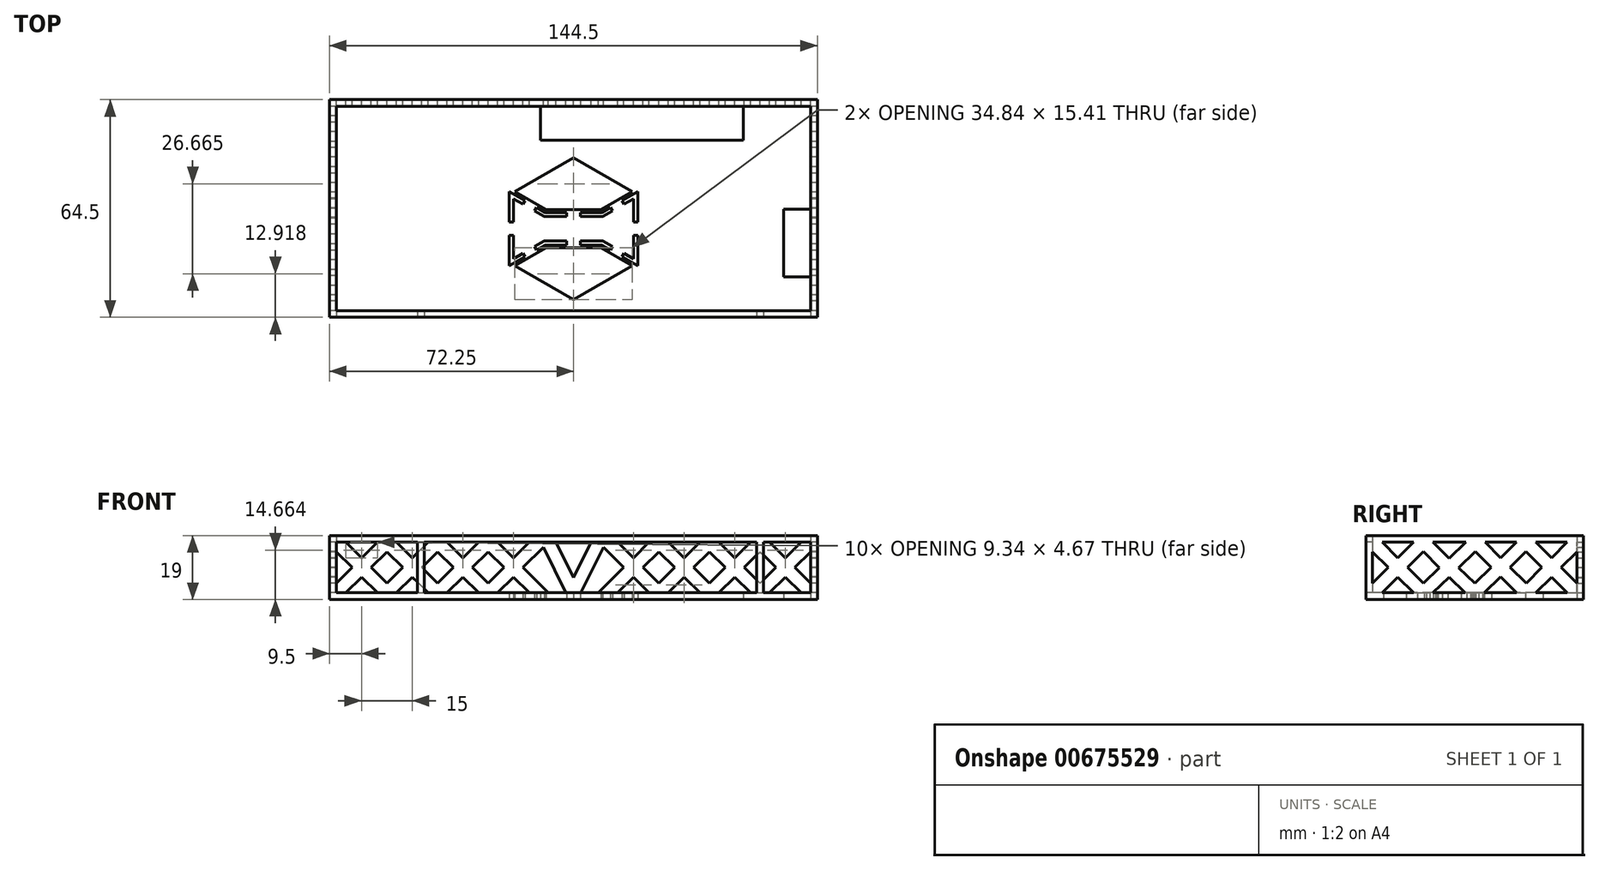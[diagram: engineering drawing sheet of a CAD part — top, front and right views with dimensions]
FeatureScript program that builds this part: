
annotation { "Feature Type Name" : "Feature", "Feature Type Description" : "" }
export const myFeature = defineFeature(function(context is Context, id is Id, definition is map)
    precondition{}
    {
        {
            var Q0;
            Q0=qCreatedBy(makeId("Top.planeOp"),FACE);
            var sketch = newSketch(context, id + "F0", { "sketchPlane" : qUnion([Q0])});
            skLineSegment(sketch, "E0.bottom", {"start": v(-72.25, 32.25) * mm, "end": v(72.25, 32.25) * mm});
            skLineSegment(sketch, "E0.top", {"start": v(-72.25, -32.25) * mm, "end": v(72.25, -32.25) * mm});
            skLineSegment(sketch, "E0.left", {"start": v(-72.25, 32.25) * mm, "end": v(-72.25, -32.25) * mm});
            skLineSegment(sketch, "E0.right", {"start": v(72.25, 32.25) * mm, "end": v(72.25, -32.25) * mm});
            skSolve(sketch);
        }
        {
            var Q0;
            Q0=qSketchRegion(id+"F0",true);
            extrude(context, id + "F1", {"entities" : qUnion([Q0]), "depth" : 2 * mm, "offsetDistance" : 25 * mm});
        }
        {
            var Q0;
            Q0=makeQuery(id+"F1.opExtrude","CAP_FACE",FACE,{"disambiguationData":[OSD([sQuery(id+"F0.wireOp",EDGE,"E0.bottom"),sQuery(id+"F0.wireOp",EDGE,"E0.top"),sQuery(id+"F0.wireOp",EDGE,"E0.left"),sQuery(id+"F0.wireOp",EDGE,"E0.right")])],"isStart":false});
            var sketch = newSketch(context, id + "F2", { "sketchPlane" : qUnion([Q0])});
            skLineSegment(sketch, "E1.0", {"start": v(-72.25, 32.25) * mm, "end": v(-72.25, -32.25) * mm});
            skLineSegment(sketch, "E1.1", {"start": v(72.25, 32.25) * mm, "end": v(-72.25, 32.25) * mm});
            skLineSegment(sketch, "E1.2", {"start": v(72.25, -32.25) * mm, "end": v(72.25, 32.25) * mm});
            skLineSegment(sketch, "E1.3", {"start": v(-72.25, -32.25) * mm, "end": v(72.25, -32.25) * mm});
            skLineSegment(sketch, "E2.0", {"start": v(-70.25, 30.25) * mm, "end": v(-70.25, -30.25) * mm});
            skLineSegment(sketch, "E2.1", {"start": v(70.25, 30.25) * mm, "end": v(-70.25, 30.25) * mm});
            skLineSegment(sketch, "E2.2", {"start": v(70.25, -30.25) * mm, "end": v(70.25, 30.25) * mm});
            skLineSegment(sketch, "E2.3", {"start": v(-70.25, -30.25) * mm, "end": v(70.25, -30.25) * mm});
            skSolve(sketch);
        }
        {
            var Q0;
            Q0=qSketchRegion(id+"F2",true);
            extrude(context, id + "F3", {"entities" : qUnion([Q0]), "operationType" : NewBodyOperationType.ADD, "depth" : 17 * mm, "offsetDistance" : 25 * mm});
        }
        {
            var Q0;
            Q0=makeQuery(id+"F3.boolean.opBoolean","MERGE",FACE,{"derivedFrom":[makeQuery(id+"F1.opExtrude","SWEPT_FACE",FACE,{"disambiguationData":[OSD([sQuery(id+"F0.wireOp",EDGE,"E0.top")])]}),makeQuery(id+"F3.opExtrude","SWEPT_FACE",FACE,{"disambiguationData":[OSD([sQuery(id+"F2.wireOp",EDGE,"E1.3")])]})]});
            var sketch = newSketch(context, id + "F4", { "sketchPlane" : qUnion([Q0])});
            skLineSegment(sketch, "E3.0", {"start": v(-70.25, 2) * mm, "end": v(-46.25, 2) * mm});
            skLineSegment(sketch, "E3.1", {"start": v(-70.25, 17) * mm, "end": v(-70.25, 2) * mm});
            skLineSegment(sketch, "E3.2", {"start": v(70.25, 17) * mm, "end": v(56.25, 17) * mm});
            skLineSegment(sketch, "E3.3", {"start": v(70.25, 2) * mm, "end": v(70.25, 17) * mm});
            skLineSegment(sketch, "E4", {"start": v(-46.25, 2) * mm, "end": v(-46.25, 17) * mm});
            skLineSegment(sketch, "E5", {"start": v(-44.25, 2) * mm, "end": v(-44.25, 17) * mm});
            skLineSegment(sketch, "E6", {"start": v(56.25, 2) * mm, "end": v(56.25, 17) * mm});
            skLineSegment(sketch, "E7", {"start": v(54.25, 2) * mm, "end": v(54.25, 17) * mm});
            skLineSegment(sketch, "E8.trimOffspring", {"start": v(54.25, 17) * mm, "end": v(-44.25, 17) * mm});
            skLineSegment(sketch, "E9.trimOffspring", {"start": v(56.25, 2) * mm, "end": v(70.25, 2) * mm});
            skLineSegment(sketch, "E10.trimOffspring", {"start": v(-46.25, 17) * mm, "end": v(-70.25, 17) * mm});
            skLineSegment(sketch, "E11.trimOffspring", {"start": v(-44.25, 2) * mm, "end": v(54.25, 2) * mm});
            skSolve(sketch);
        }
        {
            var Q0;
            Q0=qSketchRegion(id+"F4",true);
            extrude(context, id + "F5", {"entities" : qUnion([Q0]), "operationType" : NewBodyOperationType.REMOVE, "oppositeDirection" : true, "depth" : 25 * mm, "offsetDistance" : 25 * mm});
        }
        {
            var Q0;
            Q0=makeQuery(id+"F1.opExtrude","CAP_FACE",FACE,{"disambiguationData":[OSD([sQuery(id+"F0.wireOp",EDGE,"E0.bottom"),sQuery(id+"F0.wireOp",EDGE,"E0.top"),sQuery(id+"F0.wireOp",EDGE,"E0.left"),sQuery(id+"F0.wireOp",EDGE,"E0.right")])],"isStart":true});
            var sketch = newSketch(context, id + "F6", { "sketchPlane" : qUnion([Q0])});
            skLineSegment(sketch, "E12.0", {"start": v(-70.25, 30.25) * mm, "end": v(-70.25, -30.25) * mm, "construction": true});
            skLineSegment(sketch, "E12.1", {"start": v(70.25, 30.25) * mm, "end": v(-70.25, 30.25) * mm, "construction": true});
            skLineSegment(sketch, "E12.3", {"start": v(-9.75, -30.25) * mm, "end": v(50.25, -30.25) * mm});
            skLineSegment(sketch, "E13", {"start": v(50.25, -30.25) * mm, "end": v(50.25, -20.25) * mm});
            skLineSegment(sketch, "E14", {"start": v(-9.75, -30.25) * mm, "end": v(-9.75, -20.25) * mm});
            skLineSegment(sketch, "E15", {"start": v(-9.75, -20.25) * mm, "end": v(50.25, -20.25) * mm});
            skLineSegment(sketch, "E16", {"start": v(50.25, -30.25) * mm, "end": v(70.25, -30.25) * mm, "construction": true});
            skLineSegment(sketch, "E17", {"start": v(-9.75, -30.25) * mm, "end": v(-70.25, -30.25) * mm, "construction": true});
            skLineSegment(sketch, "E18", {"start": v(70.25, 20.25) * mm, "end": v(62.25, 20.25) * mm});
            skLineSegment(sketch, "E19", {"start": v(70.25, 0.25) * mm, "end": v(62.25, 0.25) * mm});
            skLineSegment(sketch, "E20", {"start": v(70.25, -30.25) * mm, "end": v(70.25, 0.25) * mm, "construction": true});
            skLineSegment(sketch, "E21", {"start": v(70.25, 20.25) * mm, "end": v(70.25, 30.25) * mm, "construction": true});
            skLineSegment(sketch, "E22", {"start": v(70.25, 20.25) * mm, "end": v(70.25, 0.25) * mm});
            skLineSegment(sketch, "E23", {"start": v(62.25, 0.25) * mm, "end": v(62.25, 20.25) * mm});
            skSolve(sketch);
        }
        {
            var Q0;
            Q0=qSketchRegion(id+"F6",true);
            extrude(context, id + "F7", {"entities" : qUnion([Q0]), "operationType" : NewBodyOperationType.REMOVE, "oppositeDirection" : true, "depth" : 25 * mm, "offsetDistance" : 25 * mm});
        }
        {
            var Q0;
            Q0=makeQuery(id+"F3.boolean.opBoolean","MERGE",FACE,{"derivedFrom":[makeQuery(id+"F1.opExtrude","SWEPT_FACE",FACE,{"disambiguationData":[OSD([sQuery(id+"F0.wireOp",EDGE,"E0.left")])]}),makeQuery(id+"F3.opExtrude","SWEPT_FACE",FACE,{"disambiguationData":[OSD([sQuery(id+"F2.wireOp",EDGE,"E1.0")])]})]});
            var sketch = newSketch(context, id + "F8", { "sketchPlane" : qUnion([Q0])});
            skLineSegment(sketch, "E24.0", {"start": v(-27.42, 2) * mm, "end": v(-18.08, 2) * mm});
            skLineSegment(sketch, "E24.1", {"start": v(-30.25, 14.17) * mm, "end": v(-30.25, 4.83) * mm});
            skLineSegment(sketch, "E24.3", {"start": v(30.25, 4.83) * mm, "end": v(30.25, 14.17) * mm});
            skLineSegment(sketch, "E25", {"start": v(-27.42, 17) * mm, "end": v(-18.08, 17) * mm});
            skLineSegment(sketch, "E26", {"start": v(-12.4, 17) * mm, "end": v(-3.08, 17) * mm});
            skLineSegment(sketch, "E27", {"start": v(2.63, 17) * mm, "end": v(12.4, 17) * mm});
            skLineSegment(sketch, "E28", {"start": v(18.08, 17) * mm, "end": v(27.42, 17) * mm});
            skLineSegment(sketch, "E29", {"start": v(-30.25, 2) * mm, "end": v(-15.25, 17) * mm, "construction": true});
            skLineSegment(sketch, "E30", {"start": v(-15.25, 17) * mm, "end": v(0, 2) * mm, "construction": true});
            skLineSegment(sketch, "E31", {"start": v(0, 2) * mm, "end": v(15.25, 17) * mm, "construction": true});
            skLineSegment(sketch, "E32", {"start": v(15.25, 17) * mm, "end": v(30.25, 2) * mm, "construction": true});
            skLineSegment(sketch, "E33", {"start": v(15.25, 17) * mm, "end": v(15.25, 2) * mm, "construction": true});
            skLineSegment(sketch, "E34", {"start": v(-0.25, 17) * mm, "end": v(0, 2) * mm, "construction": true});
            skLineSegment(sketch, "E35", {"start": v(-15.25, 17) * mm, "end": v(-15.25, 2) * mm, "construction": true});
            skLineSegment(sketch, "E36", {"start": v(-30.25, 17) * mm, "end": v(-15.25, 2) * mm, "construction": true});
            skLineSegment(sketch, "E37", {"start": v(-0.25, 17) * mm, "end": v(-15.25, 2) * mm, "construction": true});
            skLineSegment(sketch, "E38", {"start": v(30.25, 17) * mm, "end": v(15.25, 2) * mm, "construction": true});
            skLineSegment(sketch, "E39", {"start": v(-0.25, 17) * mm, "end": v(15.25, 2) * mm, "construction": true});
            skLineSegment(sketch, "E40.0", {"start": v(-27.42, 17) * mm, "end": v(-22.75, 12.33) * mm});
            skLineSegment(sketch, "E40.1", {"start": v(-3.08, 17) * mm, "end": v(-7.7, 12.38) * mm});
            skLineSegment(sketch, "E40.2", {"start": v(2.63, 17) * mm, "end": v(7.55, 12.23) * mm});
            skLineSegment(sketch, "E40.3", {"start": v(27.42, 17) * mm, "end": v(22.75, 12.33) * mm});
            skLineSegment(sketch, "E41.0", {"start": v(-30.25, 14.17) * mm, "end": v(-25.58, 9.5) * mm});
            skLineSegment(sketch, "E41.1", {"start": v(-0.23, 14.2) * mm, "end": v(-4.85, 9.57) * mm});
            skLineSegment(sketch, "E41.2", {"start": v(-0.23, 14.2) * mm, "end": v(4.7, 9.43) * mm});
            skLineSegment(sketch, "E41.3", {"start": v(30.25, 14.17) * mm, "end": v(18.08, 2) * mm});
            skLineSegment(sketch, "E42.0", {"start": v(15.24, 14.18) * mm, "end": v(19.92, 9.5) * mm});
            skLineSegment(sketch, "E42.1", {"start": v(2.85, 2) * mm, "end": v(7.57, 6.64) * mm});
            skLineSegment(sketch, "E42.2", {"start": v(-15.24, 14.18) * mm, "end": v(-10.53, 9.55) * mm});
            skLineSegment(sketch, "E42.3", {"start": v(-27.42, 2) * mm, "end": v(-22.75, 6.67) * mm});
            skLineSegment(sketch, "E43.0", {"start": v(18.08, 17) * mm, "end": v(22.75, 12.33) * mm});
            skLineSegment(sketch, "E43.1", {"start": v(0, 4.8) * mm, "end": v(4.7, 9.43) * mm});
            skLineSegment(sketch, "E43.2", {"start": v(-12.4, 17) * mm, "end": v(-7.7, 12.38) * mm});
            skLineSegment(sketch, "E43.3", {"start": v(-30.25, 4.83) * mm, "end": v(-25.58, 9.5) * mm});
            skLineSegment(sketch, "E44.trimOffspring", {"start": v(7.55, 12.23) * mm, "end": v(12.4, 17) * mm});
            skLineSegment(sketch, "E45.trimOffspring", {"start": v(7.57, 6.64) * mm, "end": v(12.37, 2) * mm});
            skLineSegment(sketch, "E46.trimOffspring", {"start": v(10.43, 9.45) * mm, "end": v(15.23, 4.8) * mm});
            skLineSegment(sketch, "E47.trimOffspring", {"start": v(22.75, 6.67) * mm, "end": v(27.42, 2) * mm});
            skLineSegment(sketch, "E48.trimOffspring", {"start": v(19.92, 9.5) * mm, "end": v(15.23, 4.8) * mm});
            skLineSegment(sketch, "E49.trimOffspring", {"start": v(25.58, 9.5) * mm, "end": v(30.25, 4.83) * mm});
            skLineSegment(sketch, "E50.trimOffspring", {"start": v(10.43, 9.45) * mm, "end": v(15.24, 14.18) * mm});
            skLineSegment(sketch, "E51.trimOffspring", {"start": v(-7.68, 6.75) * mm, "end": v(-2.85, 2) * mm});
            skLineSegment(sketch, "E52.trimOffspring", {"start": v(-7.68, 6.75) * mm, "end": v(-12.42, 2) * mm});
            skLineSegment(sketch, "E53.trimOffspring", {"start": v(-4.85, 9.57) * mm, "end": v(0, 4.8) * mm});
            skLineSegment(sketch, "E54.trimOffspring", {"start": v(-10.53, 9.55) * mm, "end": v(-15.25, 4.83) * mm});
            skLineSegment(sketch, "E55.trimOffspring", {"start": v(-19.92, 9.5) * mm, "end": v(-15.25, 4.83) * mm});
            skLineSegment(sketch, "E56.trimOffspring", {"start": v(-22.75, 12.33) * mm, "end": v(-18.08, 17) * mm});
            skLineSegment(sketch, "E57.trimOffspring", {"start": v(-22.75, 6.67) * mm, "end": v(-18.08, 2) * mm});
            skLineSegment(sketch, "E58.trimOffspring", {"start": v(-19.92, 9.5) * mm, "end": v(-15.24, 14.18) * mm});
            skLineSegment(sketch, "E59.trimOffspring", {"start": v(-12.42, 2) * mm, "end": v(-2.85, 2) * mm});
            skLineSegment(sketch, "E60.trimOffspring", {"start": v(2.85, 2) * mm, "end": v(12.37, 2) * mm});
            skLineSegment(sketch, "E61.trimOffspring", {"start": v(18.08, 2) * mm, "end": v(27.42, 2) * mm});
            skSolve(sketch);
        }
        {
            var Q0;
            Q0=qSketchRegion(id+"F8",true);
            extrude(context, id + "F9", {"entities" : qUnion([Q0]), "operationType" : NewBodyOperationType.REMOVE, "endBound" : BoundingType.THROUGH_ALL, "oppositeDirection" : true, "depth" : 25 * mm, "offsetDistance" : 25 * mm});
        }
        {
            var Q0;
            Q0=makeQuery(id+"F3.boolean.opBoolean","MERGE",FACE,{"derivedFrom":[makeQuery(id+"F1.opExtrude","SWEPT_FACE",FACE,{"disambiguationData":[OSD([sQuery(id+"F0.wireOp",EDGE,"E0.bottom")])]}),makeQuery(id+"F3.opExtrude","SWEPT_FACE",FACE,{"disambiguationData":[OSD([sQuery(id+"F2.wireOp",EDGE,"E1.1")])]})]});
            var sketch = newSketch(context, id + "F10", { "sketchPlane" : qUnion([Q0])});
            skLineSegment(sketch, "E62.0", {"start": v(-67.42, 2) * mm, "end": v(-58.08, 2) * mm});
            skLineSegment(sketch, "E62.1", {"start": v(-70.25, 14.17) * mm, "end": v(-70.25, 4.83) * mm});
            skLineSegment(sketch, "E62.2", {"start": v(67.42, 17) * mm, "end": v(58.08, 17) * mm});
            skLineSegment(sketch, "E62.3", {"start": v(70.25, 4.83) * mm, "end": v(70.25, 14.17) * mm});
            skLineSegment(sketch, "E63", {"start": v(0, 17) * mm, "end": v(0, 2) * mm, "construction": true});
            skLineSegment(sketch, "E64", {"start": v(-70.25, 17) * mm, "end": v(-55.25, 2) * mm, "construction": true});
            skLineSegment(sketch, "E65", {"start": v(-55.25, 2) * mm, "end": v(-40.25, 17) * mm, "construction": true});
            skLineSegment(sketch, "E66", {"start": v(-40.25, 17) * mm, "end": v(-25.25, 2) * mm, "construction": true});
            skLineSegment(sketch, "E67", {"start": v(-25.25, 2) * mm, "end": v(-10.25, 17) * mm, "construction": true});
            skLineSegment(sketch, "E68", {"start": v(70.25, 17) * mm, "end": v(55.25, 2) * mm, "construction": true});
            skLineSegment(sketch, "E69", {"start": v(55.25, 2) * mm, "end": v(40.25, 17) * mm, "construction": true});
            skLineSegment(sketch, "E70", {"start": v(40.25, 17) * mm, "end": v(25.25, 2) * mm, "construction": true});
            skLineSegment(sketch, "E71", {"start": v(25.25, 2) * mm, "end": v(10.25, 17) * mm, "construction": true});
            skLineSegment(sketch, "E72", {"start": v(-70.25, 2) * mm, "end": v(-55.25, 17) * mm, "construction": true});
            skLineSegment(sketch, "E73", {"start": v(-55.25, 17) * mm, "end": v(-40.25, 2) * mm, "construction": true});
            skLineSegment(sketch, "E74", {"start": v(-40.25, 2) * mm, "end": v(-25.25, 17) * mm, "construction": true});
            skLineSegment(sketch, "E75", {"start": v(-25.25, 17) * mm, "end": v(-10.25, 2) * mm, "construction": true});
            skLineSegment(sketch, "E76", {"start": v(70.25, 2) * mm, "end": v(55.25, 17) * mm, "construction": true});
            skLineSegment(sketch, "E77", {"start": v(55.25, 17) * mm, "end": v(40.25, 2) * mm, "construction": true});
            skLineSegment(sketch, "E78", {"start": v(40.25, 2) * mm, "end": v(25.25, 17) * mm, "construction": true});
            skLineSegment(sketch, "E79", {"start": v(25.25, 17) * mm, "end": v(10.25, 2) * mm, "construction": true});
            skLineSegment(sketch, "E80.0", {"start": v(-22.42, 2) * mm, "end": v(-17.75, 6.67) * mm});
            skLineSegment(sketch, "E80.1", {"start": v(-40.25, 14.17) * mm, "end": v(-35.58, 9.5) * mm});
            skLineSegment(sketch, "E80.2", {"start": v(-52.42, 2) * mm, "end": v(-47.75, 6.67) * mm});
            skLineSegment(sketch, "E80.3", {"start": v(-70.25, 14.17) * mm, "end": v(-65.58, 9.5) * mm});
            skLineSegment(sketch, "E81.0", {"start": v(-25.25, 4.83) * mm, "end": v(-20.58, 9.5) * mm});
            skLineSegment(sketch, "E81.1", {"start": v(-37.42, 17) * mm, "end": v(-32.75, 12.33) * mm});
            skLineSegment(sketch, "E81.2", {"start": v(-55.25, 4.83) * mm, "end": v(-50.58, 9.5) * mm});
            skLineSegment(sketch, "E81.3", {"start": v(-67.42, 17) * mm, "end": v(-62.75, 12.33) * mm});
            skLineSegment(sketch, "E82.0", {"start": v(-25.25, 14.17) * mm, "end": v(-20.58, 9.5) * mm});
            skLineSegment(sketch, "E82.1", {"start": v(-37.42, 2) * mm, "end": v(-25.25, 14.17) * mm});
            skLineSegment(sketch, "E82.2", {"start": v(-55.25, 14.17) * mm, "end": v(-50.58, 9.5) * mm});
            skLineSegment(sketch, "E82.3", {"start": v(-67.42, 2) * mm, "end": v(-62.75, 6.67) * mm});
            skLineSegment(sketch, "E83.0", {"start": v(-22.42, 17) * mm, "end": v(-17.75, 12.33) * mm});
            skLineSegment(sketch, "E83.1", {"start": v(-40.25, 4.83) * mm, "end": v(-35.58, 9.5) * mm});
            skLineSegment(sketch, "E83.2", {"start": v(-52.42, 17) * mm, "end": v(-47.75, 12.33) * mm});
            skLineSegment(sketch, "E83.3", {"start": v(-70.25, 4.83) * mm, "end": v(-65.58, 9.5) * mm});
            skLineSegment(sketch, "E84.0", {"start": v(25.25, 4.83) * mm, "end": v(20.58, 9.5) * mm});
            skLineSegment(sketch, "E84.1", {"start": v(37.42, 17) * mm, "end": v(32.75, 12.33) * mm});
            skLineSegment(sketch, "E84.2", {"start": v(55.25, 4.83) * mm, "end": v(50.58, 9.5) * mm});
            skLineSegment(sketch, "E84.3", {"start": v(67.42, 17) * mm, "end": v(62.75, 12.33) * mm});
            skLineSegment(sketch, "E85.0", {"start": v(22.42, 2) * mm, "end": v(17.75, 6.67) * mm});
            skLineSegment(sketch, "E85.1", {"start": v(40.25, 14.17) * mm, "end": v(35.58, 9.5) * mm});
            skLineSegment(sketch, "E85.2", {"start": v(52.42, 2) * mm, "end": v(47.75, 6.67) * mm});
            skLineSegment(sketch, "E85.3", {"start": v(70.25, 14.17) * mm, "end": v(65.58, 9.5) * mm});
            skLineSegment(sketch, "E86.0", {"start": v(22.42, 17) * mm, "end": v(17.75, 12.33) * mm});
            skLineSegment(sketch, "E86.1", {"start": v(40.25, 4.83) * mm, "end": v(35.58, 9.5) * mm});
            skLineSegment(sketch, "E86.2", {"start": v(52.42, 17) * mm, "end": v(47.75, 12.33) * mm});
            skLineSegment(sketch, "E86.3", {"start": v(70.25, 4.83) * mm, "end": v(65.58, 9.5) * mm});
            skLineSegment(sketch, "E87.0", {"start": v(25.25, 14.17) * mm, "end": v(20.58, 9.5) * mm});
            skLineSegment(sketch, "E87.1", {"start": v(37.42, 2) * mm, "end": v(32.75, 6.67) * mm});
            skLineSegment(sketch, "E87.2", {"start": v(55.25, 14.17) * mm, "end": v(50.58, 9.5) * mm});
            skLineSegment(sketch, "E87.3", {"start": v(67.42, 2) * mm, "end": v(62.75, 6.67) * mm});
            skLineSegment(sketch, "E88.trimOffspring", {"start": v(-19.16, 8.09) * mm, "end": v(-13.08, 2) * mm});
            skLineSegment(sketch, "E89.trimOffspring", {"start": v(-17.75, 12.33) * mm, "end": v(-13.08, 17) * mm});
            skLineSegment(sketch, "E90.trimOffspring", {"start": v(-14.92, 9.5) * mm, "end": v(-7.42, 2) * mm});
            skLineSegment(sketch, "E91.trimOffspring", {"start": v(-14.92, 9.5) * mm, "end": v(-8.91, 15.5) * mm});
            skLineSegment(sketch, "E92.trimOffspring", {"start": v(-32.75, 6.67) * mm, "end": v(-28.08, 2) * mm});
            skLineSegment(sketch, "E93.trimOffspring", {"start": v(-32.75, 12.33) * mm, "end": v(-28.08, 17) * mm});
            skLineSegment(sketch, "E94.trimOffspring", {"start": v(-29.92, 9.5) * mm, "end": v(-25.25, 4.83) * mm});
            skLineSegment(sketch, "E95.trimOffspring", {"start": v(-47.75, 6.67) * mm, "end": v(-43.08, 2) * mm});
            skLineSegment(sketch, "E96.trimOffspring", {"start": v(-47.75, 12.33) * mm, "end": v(-43.08, 17) * mm});
            skLineSegment(sketch, "E97.trimOffspring", {"start": v(-44.92, 9.5) * mm, "end": v(-40.25, 4.83) * mm});
            skLineSegment(sketch, "E98.trimOffspring", {"start": v(-44.92, 9.5) * mm, "end": v(-40.25, 14.17) * mm});
            skLineSegment(sketch, "E99.trimOffspring", {"start": v(-59.92, 9.5) * mm, "end": v(-55.25, 4.83) * mm});
            skLineSegment(sketch, "E100.trimOffspring", {"start": v(-59.92, 9.5) * mm, "end": v(-55.25, 14.17) * mm});
            skLineSegment(sketch, "E101.trimOffspring", {"start": v(-62.75, 6.67) * mm, "end": v(-58.08, 2) * mm});
            skLineSegment(sketch, "E102.trimOffspring", {"start": v(-62.75, 12.33) * mm, "end": v(-58.08, 17) * mm});
            skLineSegment(sketch, "E103.trimOffspring", {"start": v(14.92, 9.5) * mm, "end": v(8.91, 15.5) * mm});
            skLineSegment(sketch, "E104.trimOffspring", {"start": v(17.75, 6.67) * mm, "end": v(13.08, 2) * mm});
            skLineSegment(sketch, "E105.trimOffspring", {"start": v(17.75, 12.33) * mm, "end": v(13.08, 17) * mm});
            skLineSegment(sketch, "E106.trimOffspring", {"start": v(14.92, 9.5) * mm, "end": v(7.42, 2) * mm});
            skLineSegment(sketch, "E107.trimOffspring", {"start": v(29.92, 9.5) * mm, "end": v(25.25, 14.17) * mm});
            skLineSegment(sketch, "E108.trimOffspring", {"start": v(32.75, 6.67) * mm, "end": v(28.08, 2) * mm});
            skLineSegment(sketch, "E109.trimOffspring", {"start": v(32.75, 12.33) * mm, "end": v(28.08, 17) * mm});
            skLineSegment(sketch, "E110.trimOffspring", {"start": v(29.92, 9.5) * mm, "end": v(25.25, 4.83) * mm});
            skLineSegment(sketch, "E111.trimOffspring", {"start": v(44.92, 9.5) * mm, "end": v(40.25, 14.17) * mm});
            skLineSegment(sketch, "E112.trimOffspring", {"start": v(47.75, 6.67) * mm, "end": v(43.08, 2) * mm});
            skLineSegment(sketch, "E113.trimOffspring", {"start": v(47.75, 12.33) * mm, "end": v(43.08, 17) * mm});
            skLineSegment(sketch, "E114.trimOffspring", {"start": v(44.92, 9.5) * mm, "end": v(40.25, 4.83) * mm});
            skLineSegment(sketch, "E115.trimOffspring", {"start": v(59.92, 9.5) * mm, "end": v(55.25, 4.83) * mm});
            skLineSegment(sketch, "E116.trimOffspring", {"start": v(62.75, 12.33) * mm, "end": v(58.08, 17) * mm});
            skLineSegment(sketch, "E117.trimOffspring", {"start": v(62.75, 6.67) * mm, "end": v(58.08, 2) * mm});
            skLineSegment(sketch, "E118.trimOffspring", {"start": v(59.92, 9.5) * mm, "end": v(55.25, 14.17) * mm});
            skLineSegment(sketch, "E119.trimOffspring", {"start": v(28.08, 2) * mm, "end": v(37.42, 2) * mm});
            skLineSegment(sketch, "E120.trimOffspring", {"start": v(13.08, 2) * mm, "end": v(22.42, 2) * mm});
            skLineSegment(sketch, "E121.trimOffspring", {"start": v(5.2, 17) * mm, "end": v(-5.2, 17) * mm});
            skLineSegment(sketch, "E122.trimOffspring", {"start": v(22.42, 17) * mm, "end": v(13.08, 17) * mm});
            skLineSegment(sketch, "E123.trimOffspring", {"start": v(37.42, 17) * mm, "end": v(28.08, 17) * mm});
            skLineSegment(sketch, "E124.trimOffspring", {"start": v(43.08, 2) * mm, "end": v(52.42, 2) * mm});
            skLineSegment(sketch, "E125.trimOffspring", {"start": v(58.08, 2) * mm, "end": v(67.42, 2) * mm});
            skLineSegment(sketch, "E126.trimOffspring", {"start": v(52.42, 17) * mm, "end": v(43.08, 17) * mm});
            skLineSegment(sketch, "E127.trimOffspring", {"start": v(-7.42, 2) * mm, "end": v(-2.23, 2) * mm});
            skLineSegment(sketch, "E128.trimOffspring", {"start": v(-22.42, 2) * mm, "end": v(-13.08, 2) * mm});
            skLineSegment(sketch, "E129.trimOffspring", {"start": v(-37.42, 2) * mm, "end": v(-28.08, 2) * mm});
            skLineSegment(sketch, "E130.trimOffspring", {"start": v(-52.42, 2) * mm, "end": v(-43.08, 2) * mm});
            skLineSegment(sketch, "E131.trimOffspring", {"start": v(-58.08, 17) * mm, "end": v(-67.42, 17) * mm});
            skLineSegment(sketch, "E132.trimOffspring", {"start": v(-43.08, 17) * mm, "end": v(-52.42, 17) * mm});
            skLineSegment(sketch, "E133.trimOffspring", {"start": v(-28.08, 17) * mm, "end": v(-37.42, 17) * mm});
            skLineSegment(sketch, "E134.trimOffspring", {"start": v(-13.08, 17) * mm, "end": v(-22.42, 17) * mm});
            skLineSegment(sketch, "E135", {"start": v(-7.42, 17) * mm, "end": v(0, 2) * mm, "construction": true});
            skLineSegment(sketch, "E136", {"start": v(7.42, 17) * mm, "end": v(0, 2) * mm, "construction": true});
            skLineSegment(sketch, "E137.0", {"start": v(5.2, 17) * mm, "end": v(0, 6.5) * mm});
            skLineSegment(sketch, "E137.1", {"start": v(-5.2, 17) * mm, "end": v(0, 6.5) * mm});
            skLineSegment(sketch, "E138.0", {"start": v(8.91, 15.5) * mm, "end": v(2.23, 2) * mm});
            skLineSegment(sketch, "E138.1", {"start": v(-8.91, 15.5) * mm, "end": v(-2.23, 2) * mm});
            skLineSegment(sketch, "E139.trimOffspring", {"start": v(2.23, 2) * mm, "end": v(7.42, 2) * mm});
            skSolve(sketch);
        }
        {
            var Q0;
            Q0=qSketchRegion(id+"F10",true);
            extrude(context, id + "F11", {"entities" : qUnion([Q0]), "operationType" : NewBodyOperationType.REMOVE, "oppositeDirection" : true, "depth" : 25 * mm, "offsetDistance" : 25 * mm});
        }
        {
            var Q0;
            {var subQ0=sQuery(id+"F0.wireOp",EDGE,"E0.top");var subQ1=sQuery(id+"F0.wireOp",EDGE,"E0.right");var subQ2=sQuery(id+"F0.wireOp",EDGE,"E0.bottom");var subQ3=sQuery(id+"F0.wireOp",EDGE,"E0.left");Q0=makeQuery(id+"FJUS3B1TuTwB0FU_1.boolean.opBoolean","SPLIT",FACE,{"disambiguationData":[TD([makeQuery(id+"F1.opExtrude","SWEPT_FACE",FACE,{"disambiguationData":[OSD([subQ2])]})])],"derivedFrom":makeQuery(id+"F1.opExtrude","CAP_FACE",FACE,{"disambiguationData":[OSD([subQ2,subQ0,subQ3,subQ1])],"isStart":true})});}
            var sketch = newSketch(context, id + "F12", { "sketchPlane" : qUnion([Q0])});
            skLineSegment(sketch, "E140.1", {"start": v(9.5, 11.5) * mm, "end": v(9.5, 0.5) * mm});
            skLineSegment(sketch, "E140.4", {"start": v(-9.5, 0.5) * mm, "end": v(-9.5, 11.5) * mm});
            skLineSegment(sketch, "E141", {"start": v(-9.5, 11.5) * mm, "end": v(-4.18, 8.41) * mm});
            skLineSegment(sketch, "E142", {"start": v(9.5, 11.5) * mm, "end": v(4.18, 8.41) * mm});
            skLineSegment(sketch, "E143", {"start": v(-4.18, 3.59) * mm, "end": v(-9.5, 0.5) * mm});
            skLineSegment(sketch, "E144", {"start": v(4.18, 3.59) * mm, "end": v(9.5, 0.5) * mm});
            skLineSegment(sketch, "E145", {"start": v(-4.18, 3.59) * mm, "end": v(4.18, 3.59) * mm});
            skLineSegment(sketch, "E146", {"start": v(4.18, 8.41) * mm, "end": v(-4.18, 8.41) * mm});
            skLineSegment(sketch, "E147.0", {"start": v(4.07, 8.81) * mm, "end": v(-4.07, 8.81) * mm});
            skLineSegment(sketch, "E147.1", {"start": v(-8.7, 11.5) * mm, "end": v(-4.07, 8.81) * mm});
            skLineSegment(sketch, "E147.2", {"start": v(8.7, 11.5) * mm, "end": v(4.07, 8.81) * mm});
            skLineSegment(sketch, "E147.3", {"start": v(0, 16.52) * mm, "end": v(8.7, 11.5) * mm});
            skLineSegment(sketch, "E147.4", {"start": v(-8.7, 11.5) * mm, "end": v(0, 16.52) * mm});
            skLineSegment(sketch, "E148.0", {"start": v(0, -4.52) * mm, "end": v(-8.7, 0.5) * mm});
            skLineSegment(sketch, "E148.1", {"start": v(-4.07, 3.19) * mm, "end": v(-8.7, 0.5) * mm});
            skLineSegment(sketch, "E148.2", {"start": v(8.7, 0.5) * mm, "end": v(0, -4.52) * mm});
            skLineSegment(sketch, "E148.3", {"start": v(4.07, 3.19) * mm, "end": v(8.7, 0.5) * mm});
            skLineSegment(sketch, "E148.4", {"start": v(-4.07, 3.19) * mm, "end": v(4.07, 3.19) * mm});
            skLineSegment(sketch, "E149.0", {"start": v(-8.9, 1.55) * mm, "end": v(-8.9, 10.45) * mm});
            skLineSegment(sketch, "E149.1", {"start": v(-4.34, 4.19) * mm, "end": v(-8.9, 1.55) * mm});
            skLineSegment(sketch, "E149.2", {"start": v(-8.9, 10.45) * mm, "end": v(-4.34, 7.81) * mm});
            skLineSegment(sketch, "E149.3", {"start": v(-4.34, 4.19) * mm, "end": v(4.34, 4.19) * mm});
            skLineSegment(sketch, "E149.4", {"start": v(4.34, 7.81) * mm, "end": v(-4.34, 7.81) * mm});
            skLineSegment(sketch, "E149.5", {"start": v(8.9, 10.45) * mm, "end": v(4.34, 7.81) * mm});
            skLineSegment(sketch, "E149.6", {"start": v(8.9, 10.45) * mm, "end": v(8.9, 1.55) * mm});
            skLineSegment(sketch, "E149.7", {"start": v(4.34, 4.19) * mm, "end": v(8.9, 1.55) * mm});
            skLineSegment(sketch, "E150", {"start": v(9.5, 6) * mm, "end": v(8.9, 6) * mm, "construction": true});
            skLineSegment(sketch, "E151", {"start": v(8.9, 6) * mm, "end": v(-8.9, 6) * mm, "construction": true});
            skLineSegment(sketch, "E152", {"start": v(-8.9, 6) * mm, "end": v(-9.5, 6) * mm, "construction": true});
            skLineSegment(sketch, "E153", {"start": v(0, 16.52) * mm, "end": v(0, 8.81) * mm, "construction": true});
            skLineSegment(sketch, "E154", {"start": v(0, 8.81) * mm, "end": v(0, 8.41) * mm, "construction": true});
            skLineSegment(sketch, "E155", {"start": v(0, 8.41) * mm, "end": v(0, 7.81) * mm, "construction": true});
            skLineSegment(sketch, "E156", {"start": v(0, 7.81) * mm, "end": v(0, 4.19) * mm, "construction": true});
            skLineSegment(sketch, "E157", {"start": v(0, 4.19) * mm, "end": v(0, 3.59) * mm, "construction": true});
            skLineSegment(sketch, "E158", {"start": v(0, 3.59) * mm, "end": v(0, 3.19) * mm, "construction": true});
            skLineSegment(sketch, "E159", {"start": v(0, 3.19) * mm, "end": v(0, -4.52) * mm, "construction": true});
            skSolve(sketch);
        }
        {
            var Q0;
            Q0=qSketchRegion(id+"F12",true);
            extrude(context, id + "F13", {"entities" : qUnion([Q0]), "depth" : 1 * mm, "offsetDistance" : 25 * mm});
        }
        {
            var Q0;
            Q0=makeQuery(id+"F13.opExtrude","CAP_FACE",FACE,{"disambiguationData":[OSD([sQuery(id+"F12.wireOp",EDGE,"E140.1"),sQuery(id+"F12.wireOp",EDGE,"E140.4"),sQuery(id+"F12.wireOp",EDGE,"E141"),sQuery(id+"F12.wireOp",EDGE,"E142"),sQuery(id+"F12.wireOp",EDGE,"E143"),sQuery(id+"F12.wireOp",EDGE,"E144"),sQuery(id+"F12.wireOp",EDGE,"E145"),sQuery(id+"F12.wireOp",EDGE,"E146"),sQuery(id+"F12.wireOp",EDGE,"E149.0"),sQuery(id+"F12.wireOp",EDGE,"E149.1"),sQuery(id+"F12.wireOp",EDGE,"E149.2"),sQuery(id+"F12.wireOp",EDGE,"E149.3"),sQuery(id+"F12.wireOp",EDGE,"E149.4"),sQuery(id+"F12.wireOp",EDGE,"E149.5"),sQuery(id+"F12.wireOp",EDGE,"E149.6"),sQuery(id+"F12.wireOp",EDGE,"E149.7")])],"isStart":false});
            var sketch = newSketch(context, id + "F14", { "sketchPlane" : qUnion([Q0])});
            skPoint(sketch, "E160", {"position": v(0, 6) * mm});
            skSolve(sketch);
        }
        {
            var Q0;
            Q0=makeQuery(id+"F13.opExtrude","SWEPT_BODY",BODY,{"disambiguationData":[OSD([sQuery(id+"F12.wireOp",EDGE,"E140.1"),sQuery(id+"F12.wireOp",EDGE,"E140.4"),sQuery(id+"F12.wireOp",EDGE,"E141"),sQuery(id+"F12.wireOp",EDGE,"E142"),sQuery(id+"F12.wireOp",EDGE,"E143"),sQuery(id+"F12.wireOp",EDGE,"E144"),sQuery(id+"F12.wireOp",EDGE,"E145"),sQuery(id+"F12.wireOp",EDGE,"E146"),sQuery(id+"F12.wireOp",EDGE,"E149.0"),sQuery(id+"F12.wireOp",EDGE,"E149.1"),sQuery(id+"F12.wireOp",EDGE,"E149.2"),sQuery(id+"F12.wireOp",EDGE,"E149.3"),sQuery(id+"F12.wireOp",EDGE,"E149.4"),sQuery(id+"F12.wireOp",EDGE,"E149.5"),sQuery(id+"F12.wireOp",EDGE,"E149.6"),sQuery(id+"F12.wireOp",EDGE,"E149.7")])]});
            var Q1;
            Q1=makeQuery(id+"F13.opExtrude","SWEPT_BODY",BODY,{"disambiguationData":[OSD([sQuery(id+"F12.wireOp",EDGE,"E147.0"),sQuery(id+"F12.wireOp",EDGE,"E147.1"),sQuery(id+"F12.wireOp",EDGE,"E147.2"),sQuery(id+"F12.wireOp",EDGE,"E147.3"),sQuery(id+"F12.wireOp",EDGE,"E147.4")])]});
            var Q2;
            Q2=makeQuery(id+"F13.opExtrude","SWEPT_BODY",BODY,{"disambiguationData":[OSD([sQuery(id+"F12.wireOp",EDGE,"E148.0"),sQuery(id+"F12.wireOp",EDGE,"E148.1"),sQuery(id+"F12.wireOp",EDGE,"E148.2"),sQuery(id+"F12.wireOp",EDGE,"E148.3"),sQuery(id+"F12.wireOp",EDGE,"E148.4")])]});
            var Q3;
            Q3=sQuery(id+"F14.wireOp",VERTEX,"E160");
            transform(context, id + "F15", {"entities" : qUnion([Q0, Q1, Q2]), "transformType" : TransformType.SCALE_UNIFORMLY, "scale" : 2, "scalePoint" : qUnion([Q3]), "makeCopy" : false});
        }
        {
            var Q0;
            Q0=makeQuery(id+"F13.opExtrude","CAP_FACE",FACE,{"disambiguationData":[OSD([sQuery(id+"F12.wireOp",EDGE,"E140.1"),sQuery(id+"F12.wireOp",EDGE,"E140.4"),sQuery(id+"F12.wireOp",EDGE,"E141"),sQuery(id+"F12.wireOp",EDGE,"E142"),sQuery(id+"F12.wireOp",EDGE,"E143"),sQuery(id+"F12.wireOp",EDGE,"E144"),sQuery(id+"F12.wireOp",EDGE,"E145"),sQuery(id+"F12.wireOp",EDGE,"E146"),sQuery(id+"F12.wireOp",EDGE,"E149.0"),sQuery(id+"F12.wireOp",EDGE,"E149.1"),sQuery(id+"F12.wireOp",EDGE,"E149.2"),sQuery(id+"F12.wireOp",EDGE,"E149.3"),sQuery(id+"F12.wireOp",EDGE,"E149.4"),sQuery(id+"F12.wireOp",EDGE,"E149.5"),sQuery(id+"F12.wireOp",EDGE,"E149.6"),sQuery(id+"F12.wireOp",EDGE,"E149.7")])],"isStart":false});
            var sketch = newSketch(context, id + "F16", { "sketchPlane" : qUnion([Q0])});
            skLineSegment(sketch, "E161.0", {"start": v(-8.36, 10.83) * mm, "end": v(-19.02, 16.98) * mm});
            skLineSegment(sketch, "E161.1", {"start": v(8.36, 10.83) * mm, "end": v(-8.36, 10.83) * mm});
            skLineSegment(sketch, "E161.2", {"start": v(-19.02, 16.98) * mm, "end": v(-19.02, -4.98) * mm});
            skLineSegment(sketch, "E161.3", {"start": v(19.02, 16.98) * mm, "end": v(8.36, 10.83) * mm});
            skLineSegment(sketch, "E161.4", {"start": v(-19.02, -4.98) * mm, "end": v(-8.36, 1.17) * mm});
            skLineSegment(sketch, "E161.5", {"start": v(-8.36, 1.17) * mm, "end": v(8.36, 1.17) * mm});
            skLineSegment(sketch, "E161.6", {"start": v(8.36, 1.17) * mm, "end": v(19.02, -4.98) * mm});
            skLineSegment(sketch, "E161.7", {"start": v(19.02, -4.98) * mm, "end": v(19.02, 16.98) * mm});
            skLineSegment(sketch, "E162.0", {"start": v(-8.68, 2.37) * mm, "end": v(-17.82, -2.9) * mm});
            skLineSegment(sketch, "E162.1", {"start": v(-8.68, 2.37) * mm, "end": v(8.68, 2.37) * mm});
            skLineSegment(sketch, "E162.2", {"start": v(-17.82, -2.9) * mm, "end": v(-17.82, 14.9) * mm});
            skLineSegment(sketch, "E162.3", {"start": v(8.68, 2.37) * mm, "end": v(17.82, -2.9) * mm});
            skLineSegment(sketch, "E162.4", {"start": v(-17.82, 14.9) * mm, "end": v(-8.68, 9.63) * mm});
            skLineSegment(sketch, "E162.5", {"start": v(8.68, 9.63) * mm, "end": v(-8.68, 9.63) * mm});
            skLineSegment(sketch, "E162.6", {"start": v(17.82, 14.9) * mm, "end": v(8.68, 9.63) * mm});
            skLineSegment(sketch, "E162.7", {"start": v(17.82, 14.9) * mm, "end": v(17.82, -2.9) * mm});
            skLineSegment(sketch, "E163.0", {"start": v(-17.42, 16.98) * mm, "end": v(-8.15, 11.63) * mm});
            skLineSegment(sketch, "E163.1", {"start": v(0, 27.04) * mm, "end": v(-17.42, 16.98) * mm});
            skLineSegment(sketch, "E163.2", {"start": v(-8.15, 11.63) * mm, "end": v(8.15, 11.63) * mm});
            skLineSegment(sketch, "E163.3", {"start": v(8.15, 11.63) * mm, "end": v(17.42, 16.98) * mm});
            skLineSegment(sketch, "E163.4", {"start": v(17.42, 16.98) * mm, "end": v(0, 27.04) * mm});
            skLineSegment(sketch, "E164.0", {"start": v(-8.15, 0.37) * mm, "end": v(-17.42, -4.98) * mm});
            skLineSegment(sketch, "E164.1", {"start": v(8.15, 0.37) * mm, "end": v(-8.15, 0.37) * mm});
            skLineSegment(sketch, "E164.2", {"start": v(-17.42, -4.98) * mm, "end": v(0, -15.04) * mm});
            skLineSegment(sketch, "E164.3", {"start": v(0, -15.04) * mm, "end": v(17.42, -4.98) * mm});
            skLineSegment(sketch, "E164.4", {"start": v(17.42, -4.98) * mm, "end": v(8.15, 0.37) * mm});
            skSolve(sketch);
        }
        {
            var Q0;
            Q0=qSketchRegion(id+"F16",true);
            extrude(context, id + "F17", {"entities" : qUnion([Q0]), "operationType" : NewBodyOperationType.REMOVE, "oppositeDirection" : true, "depth" : 3 * mm, "offsetDistance" : 25 * mm});
        }
        {
            var Q0;
            Q0=makeQuery(id+"F17.boolean.opBoolean","SPLIT",FACE,{"disambiguationData":[TD([makeQuery(id+"F17.opExtrude","SWEPT_FACE",FACE,{"disambiguationData":[OSD([sQuery(id+"F16.wireOp",EDGE,"E162.0")])]})])],"derivedFrom":makeQuery(id+"F1.opExtrude","CAP_FACE",FACE,{"disambiguationData":[OSD([sQuery(id+"F0.wireOp",EDGE,"E0.bottom"),sQuery(id+"F0.wireOp",EDGE,"E0.top"),sQuery(id+"F0.wireOp",EDGE,"E0.left"),sQuery(id+"F0.wireOp",EDGE,"E0.right")])],"isStart":true})});
            var sketch = newSketch(context, id + "F18", { "sketchPlane" : qUnion([Q0])});
            skLineSegment(sketch, "E165.0", {"start": v(-2, 10.83) * mm, "end": v(2, 10.83) * mm});
            skLineSegment(sketch, "E165.1", {"start": v(14.38, 14.3) * mm, "end": v(10.92, 12.3) * mm});
            skLineSegment(sketch, "E165.2", {"start": v(-10.92, 12.3) * mm, "end": v(-14.38, 14.3) * mm});
            skLineSegment(sketch, "E165.3", {"start": v(19.02, 4) * mm, "end": v(19.02, 8) * mm});
            skLineSegment(sketch, "E165.4", {"start": v(-19.02, 4) * mm, "end": v(-19.02, 8) * mm});
            skLineSegment(sketch, "E165.5", {"start": v(-14.38, -2.3) * mm, "end": v(-10.92, -0.3) * mm});
            skLineSegment(sketch, "E165.6", {"start": v(2, 1.17) * mm, "end": v(-2, 1.17) * mm});
            skLineSegment(sketch, "E165.7", {"start": v(14.38, -2.3) * mm, "end": v(10.92, -0.3) * mm});
            skLineSegment(sketch, "E166.0", {"start": v(-2, 2.37) * mm, "end": v(2, 2.37) * mm});
            skLineSegment(sketch, "E166.1", {"start": v(-14.98, -1.26) * mm, "end": v(-11.52, 0.74) * mm});
            skLineSegment(sketch, "E166.2", {"start": v(11.52, 0.74) * mm, "end": v(14.98, -1.26) * mm});
            skLineSegment(sketch, "E166.3", {"start": v(-17.82, 8) * mm, "end": v(-17.82, 4) * mm});
            skLineSegment(sketch, "E166.4", {"start": v(17.82, 4) * mm, "end": v(17.82, 8) * mm});
            skLineSegment(sketch, "E166.5", {"start": v(14.98, 13.26) * mm, "end": v(11.52, 11.26) * mm});
            skLineSegment(sketch, "E166.6", {"start": v(2, 9.63) * mm, "end": v(-2, 9.63) * mm});
            skLineSegment(sketch, "E166.7", {"start": v(-11.52, 11.26) * mm, "end": v(-14.98, 13.26) * mm});
            skLineSegment(sketch, "E167", {"start": v(-17.82, 6) * mm, "end": v(-19.02, 6) * mm, "construction": true});
            skLineSegment(sketch, "E168", {"start": v(-17.82, 8) * mm, "end": v(-19.02, 8) * mm});
            skLineSegment(sketch, "E169", {"start": v(-17.82, 4) * mm, "end": v(-19.02, 4) * mm});
            skLineSegment(sketch, "E170", {"start": v(17.82, 6) * mm, "end": v(19.02, 6) * mm, "construction": true});
            skLineSegment(sketch, "E171", {"start": v(17.82, 8) * mm, "end": v(19.02, 8) * mm});
            skLineSegment(sketch, "E172", {"start": v(17.82, 4) * mm, "end": v(19.02, 4) * mm});
            skLineSegment(sketch, "E173", {"start": v(0, 9.63) * mm, "end": v(0, 10.83) * mm, "construction": true});
            skLineSegment(sketch, "E174", {"start": v(-13.25, -0.26) * mm, "end": v(-12.65, -1.3) * mm, "construction": true});
            skLineSegment(sketch, "E175", {"start": v(-13.25, 12.26) * mm, "end": v(-12.65, 13.3) * mm, "construction": true});
            skLineSegment(sketch, "E176", {"start": v(13.25, 12.26) * mm, "end": v(12.65, 13.3) * mm, "construction": true});
            skLineSegment(sketch, "E177", {"start": v(13.25, -0.26) * mm, "end": v(12.65, -1.3) * mm, "construction": true});
            skLineSegment(sketch, "E178", {"start": v(2, 1.17) * mm, "end": v(2, 2.37) * mm});
            skLineSegment(sketch, "E179", {"start": v(11.52, 0.74) * mm, "end": v(10.92, -0.3) * mm});
            skLineSegment(sketch, "E180", {"start": v(14.98, -1.26) * mm, "end": v(14.38, -2.3) * mm});
            skLineSegment(sketch, "E181", {"start": v(11.52, 11.26) * mm, "end": v(10.92, 12.3) * mm});
            skLineSegment(sketch, "E182", {"start": v(14.98, 13.26) * mm, "end": v(14.38, 14.3) * mm});
            skLineSegment(sketch, "E183", {"start": v(2, 9.63) * mm, "end": v(2, 10.83) * mm});
            skLineSegment(sketch, "E184", {"start": v(-2, 9.63) * mm, "end": v(-2, 10.83) * mm});
            skLineSegment(sketch, "E185", {"start": v(-11.52, 11.26) * mm, "end": v(-10.92, 12.3) * mm});
            skLineSegment(sketch, "E186", {"start": v(-14.98, 13.26) * mm, "end": v(-14.38, 14.3) * mm});
            skLineSegment(sketch, "E187", {"start": v(-11.52, 0.74) * mm, "end": v(-10.92, -0.3) * mm});
            skLineSegment(sketch, "E188", {"start": v(-14.98, -1.26) * mm, "end": v(-14.38, -2.3) * mm});
            skLineSegment(sketch, "E189", {"start": v(-2, 2.37) * mm, "end": v(-2, 1.17) * mm});
            skLineSegment(sketch, "E190", {"start": v(0, 2.37) * mm, "end": v(0, 1.17) * mm, "construction": true});
            skSolve(sketch);
        }
        {
            var Q0;
            Q0=qSketchRegion(id+"F18",true);
            extrude(context, id + "F19", {"entities" : qUnion([Q0]), "oppositeDirection" : true, "depth" : 2 * mm, "offsetDistance" : 25 * mm});
        }
        {
            var Q0;
            Q0=makeQuery(id+"F17.boolean.opBoolean","SPLIT",BODY,{"disambiguationData":[OD(0.0)],"derivedFrom":makeQuery(id+"F1.opExtrude","SWEPT_BODY",BODY,{"disambiguationData":[OSD([sQuery(id+"F0.wireOp",EDGE,"E0.bottom"),sQuery(id+"F0.wireOp",EDGE,"E0.top"),sQuery(id+"F0.wireOp",EDGE,"E0.left"),sQuery(id+"F0.wireOp",EDGE,"E0.right")])]})});
            var Q1;
            Q1=makeQuery(id+"F17.boolean.opBoolean","SPLIT",BODY,{"disambiguationData":[OD(1.0)],"derivedFrom":makeQuery(id+"F1.opExtrude","SWEPT_BODY",BODY,{"disambiguationData":[OSD([sQuery(id+"F0.wireOp",EDGE,"E0.bottom"),sQuery(id+"F0.wireOp",EDGE,"E0.top"),sQuery(id+"F0.wireOp",EDGE,"E0.left"),sQuery(id+"F0.wireOp",EDGE,"E0.right")])]})});
            var Q2;
            Q2=makeQuery(id+"F19.opExtrude","SWEPT_BODY",BODY,{"disambiguationData":[OSD([sQuery(id+"F18.wireOp",EDGE,"E165.0"),sQuery(id+"F18.wireOp",EDGE,"E166.6"),sQuery(id+"F18.wireOp",EDGE,"E183"),sQuery(id+"F18.wireOp",EDGE,"E184")])]});
            var Q3;
            Q3=makeQuery(id+"F19.opExtrude","SWEPT_BODY",BODY,{"disambiguationData":[OSD([sQuery(id+"F18.wireOp",EDGE,"E165.1"),sQuery(id+"F18.wireOp",EDGE,"E166.5"),sQuery(id+"F18.wireOp",EDGE,"E181"),sQuery(id+"F18.wireOp",EDGE,"E182")])]});
            var Q4;
            Q4=makeQuery(id+"F19.opExtrude","SWEPT_BODY",BODY,{"disambiguationData":[OSD([sQuery(id+"F18.wireOp",EDGE,"E165.2"),sQuery(id+"F18.wireOp",EDGE,"E166.7"),sQuery(id+"F18.wireOp",EDGE,"E185"),sQuery(id+"F18.wireOp",EDGE,"E186")])]});
            var Q5;
            Q5=makeQuery(id+"F19.opExtrude","SWEPT_BODY",BODY,{"disambiguationData":[OSD([sQuery(id+"F18.wireOp",EDGE,"E165.3"),sQuery(id+"F18.wireOp",EDGE,"E166.4"),sQuery(id+"F18.wireOp",EDGE,"E171"),sQuery(id+"F18.wireOp",EDGE,"E172")])]});
            var Q6;
            Q6=makeQuery(id+"F19.opExtrude","SWEPT_BODY",BODY,{"disambiguationData":[OSD([sQuery(id+"F18.wireOp",EDGE,"E165.4"),sQuery(id+"F18.wireOp",EDGE,"E166.3"),sQuery(id+"F18.wireOp",EDGE,"E168"),sQuery(id+"F18.wireOp",EDGE,"E169")])]});
            var Q7;
            Q7=makeQuery(id+"F19.opExtrude","SWEPT_BODY",BODY,{"disambiguationData":[OSD([sQuery(id+"F18.wireOp",EDGE,"E165.5"),sQuery(id+"F18.wireOp",EDGE,"E166.1"),sQuery(id+"F18.wireOp",EDGE,"E187"),sQuery(id+"F18.wireOp",EDGE,"E188")])]});
            var Q8;
            Q8=makeQuery(id+"F19.opExtrude","SWEPT_BODY",BODY,{"disambiguationData":[OSD([sQuery(id+"F18.wireOp",EDGE,"E165.6"),sQuery(id+"F18.wireOp",EDGE,"E166.0"),sQuery(id+"F18.wireOp",EDGE,"E178"),sQuery(id+"F18.wireOp",EDGE,"E189")])]});
            var Q9;
            Q9=makeQuery(id+"F19.opExtrude","SWEPT_BODY",BODY,{"disambiguationData":[OSD([sQuery(id+"F18.wireOp",EDGE,"E165.7"),sQuery(id+"F18.wireOp",EDGE,"E166.2"),sQuery(id+"F18.wireOp",EDGE,"E179"),sQuery(id+"F18.wireOp",EDGE,"E180")])]});
            booleanBodies(context, id + "F20", {"operationType" : BooleanOperationType.UNION, "tools" : qUnion([Q0, Q1, Q2, Q3, Q4, Q5, Q6, Q7, Q8, Q9])});
        }
        {
            var Q0;
            {var subQ0=sQuery(id+"F0.wireOp",EDGE,"E0.top");var subQ1=sQuery(id+"F0.wireOp",EDGE,"E0.right");var subQ2=sQuery(id+"F0.wireOp",EDGE,"E0.bottom");var subQ3=sQuery(id+"F0.wireOp",EDGE,"E0.left");var subQ4=makeQuery(id+"F1.opExtrude","CAP_FACE",FACE,{"disambiguationData":[OSD([subQ2,subQ0,subQ3,subQ1])],"isStart":true});Q0=makeQuery(id+"F20.opBoolean","MERGE",FACE,{"derivedFrom":[makeQuery(id+"F17.boolean.opBoolean","SPLIT",FACE,{"disambiguationData":[TD([makeQuery(id+"F17.opExtrude","SWEPT_FACE",FACE,{"disambiguationData":[OSD([sQuery(id+"F16.wireOp",EDGE,"E162.0")])]})])],"derivedFrom":subQ4}),makeQuery(id+"F17.boolean.opBoolean","SPLIT",FACE,{"disambiguationData":[TD([makeQuery(id+"F1.opExtrude","SWEPT_FACE",FACE,{"disambiguationData":[OSD([subQ2])]})])],"derivedFrom":subQ4}),makeQuery(id+"F19.opExtrude","CAP_FACE",FACE,{"disambiguationData":[OSD([sQuery(id+"F18.wireOp",EDGE,"E165.0"),sQuery(id+"F18.wireOp",EDGE,"E166.6"),sQuery(id+"F18.wireOp",EDGE,"E183"),sQuery(id+"F18.wireOp",EDGE,"E184")])],"isStart":true}),makeQuery(id+"F19.opExtrude","CAP_FACE",FACE,{"disambiguationData":[OSD([sQuery(id+"F18.wireOp",EDGE,"E165.1"),sQuery(id+"F18.wireOp",EDGE,"E166.5"),sQuery(id+"F18.wireOp",EDGE,"E181"),sQuery(id+"F18.wireOp",EDGE,"E182")])],"isStart":true}),makeQuery(id+"F19.opExtrude","CAP_FACE",FACE,{"disambiguationData":[OSD([sQuery(id+"F18.wireOp",EDGE,"E165.2"),sQuery(id+"F18.wireOp",EDGE,"E166.7"),sQuery(id+"F18.wireOp",EDGE,"E185"),sQuery(id+"F18.wireOp",EDGE,"E186")])],"isStart":true}),makeQuery(id+"F19.opExtrude","CAP_FACE",FACE,{"disambiguationData":[OSD([sQuery(id+"F18.wireOp",EDGE,"E165.3"),sQuery(id+"F18.wireOp",EDGE,"E166.4"),sQuery(id+"F18.wireOp",EDGE,"E171"),sQuery(id+"F18.wireOp",EDGE,"E172")])],"isStart":true}),makeQuery(id+"F19.opExtrude","CAP_FACE",FACE,{"disambiguationData":[OSD([sQuery(id+"F18.wireOp",EDGE,"E165.4"),sQuery(id+"F18.wireOp",EDGE,"E166.3"),sQuery(id+"F18.wireOp",EDGE,"E168"),sQuery(id+"F18.wireOp",EDGE,"E169")])],"isStart":true}),makeQuery(id+"F19.opExtrude","CAP_FACE",FACE,{"disambiguationData":[OSD([sQuery(id+"F18.wireOp",EDGE,"E165.5"),sQuery(id+"F18.wireOp",EDGE,"E166.1"),sQuery(id+"F18.wireOp",EDGE,"E187"),sQuery(id+"F18.wireOp",EDGE,"E188")])],"isStart":true}),makeQuery(id+"F19.opExtrude","CAP_FACE",FACE,{"disambiguationData":[OSD([sQuery(id+"F18.wireOp",EDGE,"E165.6"),sQuery(id+"F18.wireOp",EDGE,"E166.0"),sQuery(id+"F18.wireOp",EDGE,"E178"),sQuery(id+"F18.wireOp",EDGE,"E189")])],"isStart":true}),makeQuery(id+"F19.opExtrude","CAP_FACE",FACE,{"disambiguationData":[OSD([sQuery(id+"F18.wireOp",EDGE,"E165.7"),sQuery(id+"F18.wireOp",EDGE,"E166.2"),sQuery(id+"F18.wireOp",EDGE,"E179"),sQuery(id+"F18.wireOp",EDGE,"E180")])],"isStart":true})]});}
            var sketch = newSketch(context, id + "F21", { "sketchPlane" : qUnion([Q0])});
            skLineSegment(sketch, "E191.0", {"start": v(0, 27.04) * mm, "end": v(17.42, 16.98) * mm});
            skLineSegment(sketch, "E191.1", {"start": v(-17.42, 16.98) * mm, "end": v(0, 27.04) * mm});
            skLineSegment(sketch, "E191.2", {"start": v(17.42, 16.98) * mm, "end": v(8.15, 11.63) * mm});
            skLineSegment(sketch, "E191.3", {"start": v(8.15, 11.63) * mm, "end": v(-8.15, 11.63) * mm});
            skLineSegment(sketch, "E191.4", {"start": v(-8.15, 11.63) * mm, "end": v(-17.42, 16.98) * mm});
            skLineSegment(sketch, "E192.0", {"start": v(-14.98, 13.26) * mm, "end": v(-14.38, 14.3) * mm});
            skLineSegment(sketch, "E192.1", {"start": v(-17.82, 14.9) * mm, "end": v(-17.82, 8) * mm});
            skLineSegment(sketch, "E192.2", {"start": v(-17.82, 8) * mm, "end": v(-19.02, 8) * mm});
            skLineSegment(sketch, "E192.3", {"start": v(-14.98, 13.26) * mm, "end": v(-17.82, 14.9) * mm});
            skLineSegment(sketch, "E192.4", {"start": v(-19.02, 16.98) * mm, "end": v(-19.02, 8) * mm});
            skLineSegment(sketch, "E192.5", {"start": v(-14.38, 14.3) * mm, "end": v(-19.02, 16.98) * mm});
            skLineSegment(sketch, "E193.0", {"start": v(-2, 2.37) * mm, "end": v(-2, 1.17) * mm});
            skLineSegment(sketch, "E193.1", {"start": v(-10.92, -0.3) * mm, "end": v(-8.36, 1.17) * mm});
            skLineSegment(sketch, "E193.2", {"start": v(-11.52, 0.74) * mm, "end": v(-10.92, -0.3) * mm});
            skLineSegment(sketch, "E193.3", {"start": v(-2, 1.17) * mm, "end": v(-8.36, 1.17) * mm});
            skLineSegment(sketch, "E193.4", {"start": v(-11.52, 0.74) * mm, "end": v(-8.68, 2.37) * mm});
            skLineSegment(sketch, "E193.5", {"start": v(-2, 2.37) * mm, "end": v(-8.68, 2.37) * mm});
            skLineSegment(sketch, "E194.0", {"start": v(10.92, -0.3) * mm, "end": v(8.36, 1.17) * mm});
            skLineSegment(sketch, "E194.1", {"start": v(2, 1.17) * mm, "end": v(2, 2.37) * mm});
            skLineSegment(sketch, "E194.2", {"start": v(8.68, 2.37) * mm, "end": v(2, 2.37) * mm});
            skLineSegment(sketch, "E194.3", {"start": v(8.36, 1.17) * mm, "end": v(2, 1.17) * mm});
            skLineSegment(sketch, "E194.4", {"start": v(11.52, 0.74) * mm, "end": v(8.68, 2.37) * mm});
            skLineSegment(sketch, "E194.5", {"start": v(11.52, 0.74) * mm, "end": v(10.92, -0.3) * mm});
            skLineSegment(sketch, "E195.0", {"start": v(17.82, -2.9) * mm, "end": v(17.82, 4) * mm});
            skLineSegment(sketch, "E195.1", {"start": v(14.98, -1.26) * mm, "end": v(14.38, -2.3) * mm});
            skLineSegment(sketch, "E195.2", {"start": v(19.02, -4.98) * mm, "end": v(14.38, -2.3) * mm});
            skLineSegment(sketch, "E195.3", {"start": v(17.82, -2.9) * mm, "end": v(14.98, -1.26) * mm});
            skLineSegment(sketch, "E195.4", {"start": v(19.02, -4.98) * mm, "end": v(19.02, 4) * mm});
            skLineSegment(sketch, "E195.5", {"start": v(17.82, 4) * mm, "end": v(19.02, 4) * mm});
            skLineSegment(sketch, "E196.0", {"start": v(2, 9.63) * mm, "end": v(8.68, 9.63) * mm});
            skLineSegment(sketch, "E196.1", {"start": v(11.52, 11.26) * mm, "end": v(10.92, 12.3) * mm});
            skLineSegment(sketch, "E196.2", {"start": v(8.36, 10.83) * mm, "end": v(10.92, 12.3) * mm});
            skLineSegment(sketch, "E196.3", {"start": v(8.68, 9.63) * mm, "end": v(11.52, 11.26) * mm});
            skLineSegment(sketch, "E196.4", {"start": v(2, 10.83) * mm, "end": v(8.36, 10.83) * mm});
            skLineSegment(sketch, "E196.5", {"start": v(2, 9.63) * mm, "end": v(2, 10.83) * mm});
            skLineSegment(sketch, "E197.0", {"start": v(-8.68, 9.63) * mm, "end": v(-11.52, 11.26) * mm});
            skLineSegment(sketch, "E197.1", {"start": v(-2, 9.63) * mm, "end": v(-2, 10.83) * mm});
            skLineSegment(sketch, "E197.2", {"start": v(-8.36, 10.83) * mm, "end": v(-2, 10.83) * mm});
            skLineSegment(sketch, "E197.3", {"start": v(-8.68, 9.63) * mm, "end": v(-2, 9.63) * mm});
            skLineSegment(sketch, "E197.4", {"start": v(-8.36, 10.83) * mm, "end": v(-10.92, 12.3) * mm});
            skLineSegment(sketch, "E197.5", {"start": v(-11.52, 11.26) * mm, "end": v(-10.92, 12.3) * mm});
            skLineSegment(sketch, "E198.0", {"start": v(8.15, 0.37) * mm, "end": v(17.42, -4.98) * mm});
            skLineSegment(sketch, "E198.1", {"start": v(-8.15, 0.37) * mm, "end": v(8.15, 0.37) * mm});
            skLineSegment(sketch, "E198.2", {"start": v(17.42, -4.98) * mm, "end": v(0, -15.04) * mm});
            skLineSegment(sketch, "E198.3", {"start": v(0, -15.04) * mm, "end": v(-17.42, -4.98) * mm});
            skLineSegment(sketch, "E198.4", {"start": v(-17.42, -4.98) * mm, "end": v(-8.15, 0.37) * mm});
            skLineSegment(sketch, "E199.0", {"start": v(-17.82, -2.9) * mm, "end": v(-14.98, -1.26) * mm});
            skLineSegment(sketch, "E199.1", {"start": v(-19.02, -4.98) * mm, "end": v(-14.38, -2.3) * mm});
            skLineSegment(sketch, "E199.2", {"start": v(-19.02, 4) * mm, "end": v(-19.02, -4.98) * mm});
            skLineSegment(sketch, "E199.3", {"start": v(-14.98, -1.26) * mm, "end": v(-14.38, -2.3) * mm});
            skLineSegment(sketch, "E199.4", {"start": v(-17.82, 4) * mm, "end": v(-19.02, 4) * mm});
            skLineSegment(sketch, "E199.5", {"start": v(-17.82, 4) * mm, "end": v(-17.82, -2.9) * mm});
            skLineSegment(sketch, "E200.0", {"start": v(17.82, 8) * mm, "end": v(19.02, 8) * mm});
            skLineSegment(sketch, "E200.1", {"start": v(14.98, 13.26) * mm, "end": v(17.82, 14.9) * mm});
            skLineSegment(sketch, "E200.2", {"start": v(14.98, 13.26) * mm, "end": v(14.38, 14.3) * mm});
            skLineSegment(sketch, "E200.3", {"start": v(17.82, 8) * mm, "end": v(17.82, 14.9) * mm});
            skLineSegment(sketch, "E200.4", {"start": v(14.38, 14.3) * mm, "end": v(19.02, 16.98) * mm});
            skLineSegment(sketch, "E200.5", {"start": v(19.02, 8) * mm, "end": v(19.02, 16.98) * mm});
            skSolve(sketch);
        }
        {
            var Q0;
            Q0 = qSketchRegion(id + "F21", true);
            extrude(context, id + "F22", {"entities" : qUnion([Q0]), "oppositeDirection" : true, "depth" : 2 * mm, "offsetDistance" : 25 * mm});
        }
    });
